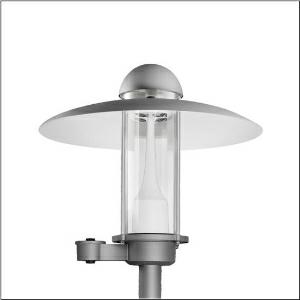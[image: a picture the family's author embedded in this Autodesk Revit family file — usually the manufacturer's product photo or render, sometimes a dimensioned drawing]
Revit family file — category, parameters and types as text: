
# Revit family: city-light_elegance_iq___st1_2a_5xa5265ey14h000022_f597
name_source: partatom
category: Lighting Fixtures
units: mm (PartAtom-declared; Revit-internal decimal feet)

## family parameters
Cut with Voids When Loaded = No
Host = Face
Light Source = No
Part Type = Normal
Room Calculation Point = No
Round Connector Dimension = Use Diameter
Shared = No

## types (1)
- --- (1 x LED, 1460 lm, 10.7 W, 3000K)
    Apparent Load = 11 VA
    CIE Flux Codes = 22 62 94 98 100
    Color Rendering = 70
    Color Temperature = 3000K
    Default Elevation = 1800 mm
    Description = City-Light Elegance iQ, mast luminaire, Module 540 iQ-SR, primary light control with 3 zone facetted reflector, of plastic, silver coated, highly specular, structured, primary optical cover: cover, of PMMA, transparent, light distribution: ST1.2a, light emission: direct distribution, primary light characteristic: asymmetric, installation type: post-top, LED, High Power LED, rated luminous flux: 1.460lm, luminous efficacy: 136lm/W, light colour: 730, colour temperature: 3000K, control gear: iQ-Street Remote, D4i with power reduction, control: optimised constant luminous flux control (CLO 2.0), Desk-Remote (wireless, voltage-free reading and setting of iQ features in the workshop via application-optimized NFC function/RFID function), Light-Fading, Smart-Wire, Night-Set, Lumen-Switch, Temp-Guard, Auto-Match, Street-Remote, pre-setting: logarithmic dimming characteristic, with terminal, 6-pole, max. 2.5mm², mains connection: 230..240V, AC, 50/60Hz, connection cable pre-assembled, cable length: 5,5m, wiring characteristics: H07RN-F, start of lifetime: 11W, end of service life: 11W, reduction: 6W, luminaire housing, upper part, of aluminium, coated, Siteco® metallic grey (DB 702S), diameter: 750mm, height: 675mm, spigot size: d x l = 76 x 70mm (post-top) | with reducer (optional accessory) 60 x 70mm, mounting height: 3..5m, post-top mast mounting element, of diecast aluminium, coated, Siteco® metallic grey (DB 702S), Module 540 iQ-SR, traffic white (RAL 9016), equipment: standard, Smart Interface below and above, protection rating (complete): IP65, insulation class (complete): insulation class II (safety insulation), certification: CE, ENEC, VDE, packaging unit: 1 piece

Light Distribution: ST1.2a
    Height = 675 mm
    Lamp = 1 x LED
    Lamp Light Flux = 1460 lm
    Lamp Power = 10.7 W
    Lamp count = 1
    Length = 750 mm
    Luminous efficacy = 136 lm/W
    Manufacturer = Siteco
    ModVariant = No
    Model = 5XA5265EY14H000022
    Number of Poles = 1
    OnlyDefault = Yes
    Power Factor = 1
    Product Name = City-Light Elegance iQ | ST1.2a
    Product group = mast luminaire | pylon top
    ProductGroupID = 6100
    Protection Class = Protection class II
    Protection Degree = IP 65
    RLX_Detail_Level = 1
    RLX_Emergency_Light_Flux = 0 lm
    RLX_Emergency_Type = 0
    RLX_Emergency_Type_DB = No
    RlxData = <blob elided: 72741 chars, md5=21f8678a>
    Socket = socket
    Standby Power = 0 W
    System Light Flux = 1460 lm
    System Power = 11 W
    Type Comments = factory setting: luminous flux: 100 % | dim-lin: 254 | 419 mA
    Type Image = l_1005991.jpg
    URL = http://relux.com
    VarID = @adj_107869
    Voltage = 0 V
    Weight = 0.00 kg
    Width = 0 mm  [stored 0 ft]

note: [stored X ft] marks values corroborated as IEEE doubles in the binary element streams (Revit-internal decimal feet)

## geometry (parser evidence)
native form markers: Blend x4, Sweep x9
no freeform markers — native parametric forms only
